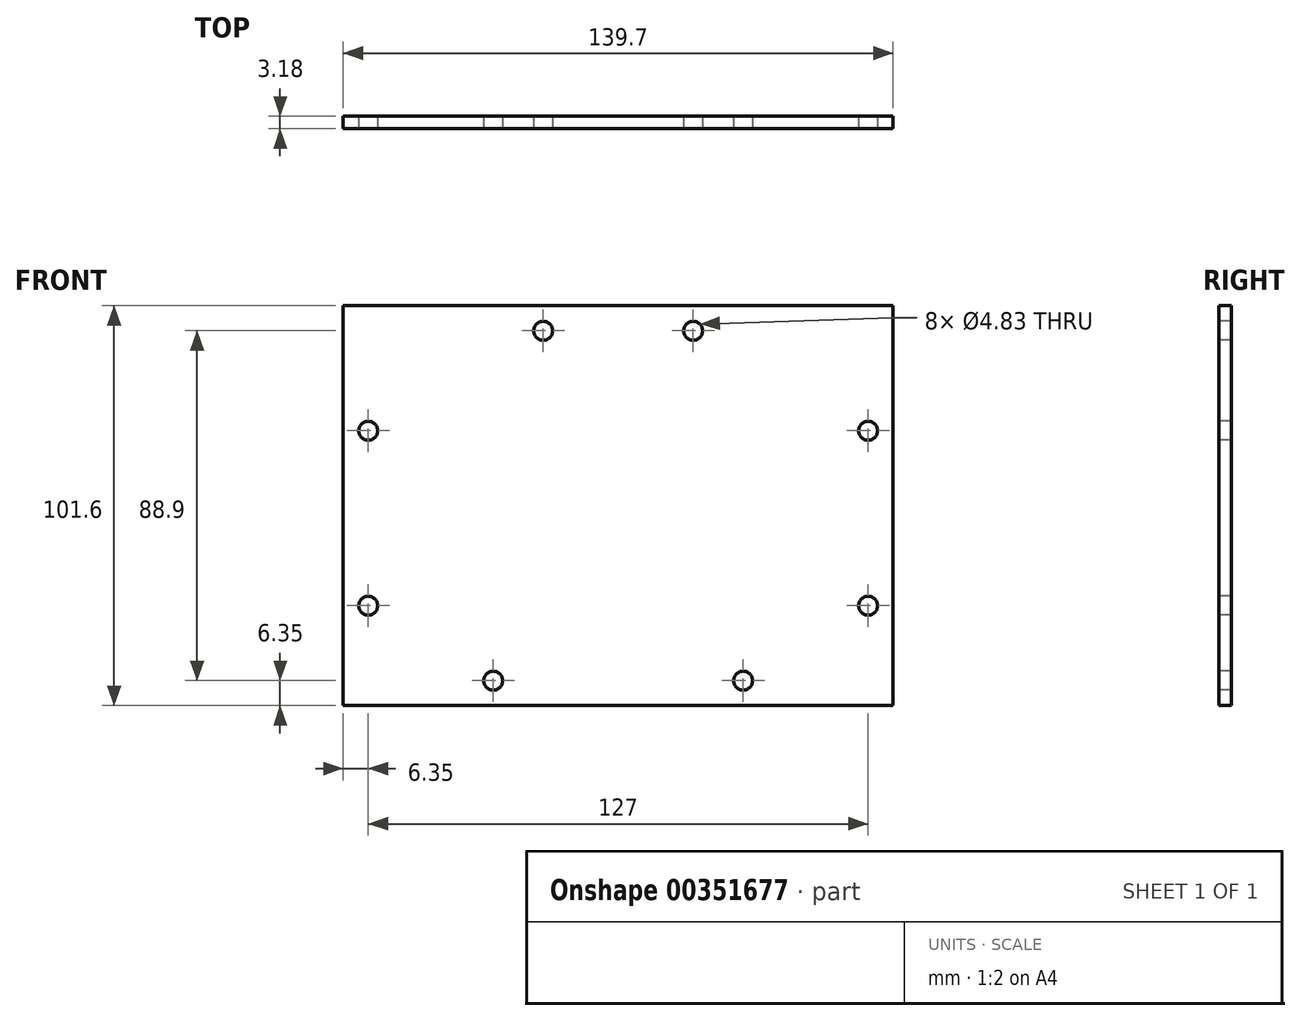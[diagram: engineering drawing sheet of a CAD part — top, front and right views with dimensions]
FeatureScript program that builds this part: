
annotation { "Feature Type Name" : "Feature", "Feature Type Description" : "" }
export const myFeature = defineFeature(function(context is Context, id is Id, definition is map)
    precondition{}
    {
        {
            var Q0;
            Q0=qCreatedBy(makeId("Front.planeOp"),FACE);
            var sketch = newSketch(context, id + "F0", { "sketchPlane" : qUnion([Q0])});
            skLineSegment(sketch, "E0.bottom", {"start": v(-69.85, 50.8) * mm, "end": v(69.85, 50.8) * mm});
            skLineSegment(sketch, "E0.top", {"start": v(-69.85, -50.8) * mm, "end": v(69.85, -50.8) * mm});
            skLineSegment(sketch, "E0.left", {"start": v(-69.85, 50.8) * mm, "end": v(-69.85, -50.8) * mm});
            skLineSegment(sketch, "E0.right", {"start": v(69.85, 50.8) * mm, "end": v(69.85, -50.8) * mm});
            skPoint(sketch, "E0.middle", {"position": v(0, 0) * mm});
            skSolve(sketch);
        }
        {
            var Q0;
            Q0 = qSketchRegion(id + "F0", true);
            extrude(context, id + "F1", {"entities" : qUnion([Q0]), "endBound" : BoundingType.SYMMETRIC, "depth" : 3.17 * mm});
        }
        {
            var Q0;
            Q0=makeQuery(id+"F1.opExtrude","CAP_FACE",FACE,{"disambiguationData":[OSD([sQuery(id+"F0.wireOp",EDGE,"E0.bottom"),sQuery(id+"F0.wireOp",EDGE,"E0.top"),sQuery(id+"F0.wireOp",EDGE,"E0.left"),sQuery(id+"F0.wireOp",EDGE,"E0.right")])],"isStart":false});
            var sketch = newSketch(context, id + "F2", { "sketchPlane" : qUnion([Q0])});
            skCircle(sketch, "E1", {"center": v(-19.05, 44.45) * mm, "radius": 2.41 * mm});
            skCircle(sketch, "E2", {"center": v(19.05, 44.45) * mm, "radius": 2.41 * mm});
            skSolve(sketch);
        }
        {
            var Q0;
            Q0 = qSketchRegion(id + "F2", true);
            extrude(context, id + "F3", {"entities" : qUnion([Q0]), "operationType" : NewBodyOperationType.REMOVE, "oppositeDirection" : true, "depth" : 3.17 * mm});
        }
        {
            var Q0;
            Q0=makeQuery(id+"F1.opExtrude","CAP_FACE",FACE,{"disambiguationData":[OSD([sQuery(id+"F0.wireOp",EDGE,"E0.bottom"),sQuery(id+"F0.wireOp",EDGE,"E0.top"),sQuery(id+"F0.wireOp",EDGE,"E0.left"),sQuery(id+"F0.wireOp",EDGE,"E0.right")])],"isStart":false});
            var sketch = newSketch(context, id + "F4", { "sketchPlane" : qUnion([Q0])});
            skCircle(sketch, "E3", {"center": v(63.5, 19.05) * mm, "radius": 2.41 * mm});
            skCircle(sketch, "E4", {"center": v(63.5, -25.4) * mm, "radius": 2.41 * mm});
            skSolve(sketch);
        }
        {
            var Q0;
            Q0 = qSketchRegion(id + "F4", true);
            extrude(context, id + "F5", {"entities" : qUnion([Q0]), "operationType" : NewBodyOperationType.REMOVE, "oppositeDirection" : true, "depth" : 3.17 * mm});
        }
        {
            var Q0;
            Q0=makeQuery(id+"F1.opExtrude","CAP_FACE",FACE,{"disambiguationData":[OSD([sQuery(id+"F0.wireOp",EDGE,"E0.bottom"),sQuery(id+"F0.wireOp",EDGE,"E0.top"),sQuery(id+"F0.wireOp",EDGE,"E0.left"),sQuery(id+"F0.wireOp",EDGE,"E0.right")])],"isStart":false});
            var sketch = newSketch(context, id + "F6", { "sketchPlane" : qUnion([Q0])});
            skCircle(sketch, "E5", {"center": v(-31.75, -44.45) * mm, "radius": 2.41 * mm});
            skSolve(sketch);
        }
        {
            var Q0;
            Q0=makeQuery(id+"F6.imprint","IMPRINT",FACE,{"disambiguationData":[TD([[makeQuery(id+"F6.imprint","IMPRINT",EDGE,{"derivedFrom":sQuery(id+"F6.wireOp",EDGE,"E5")}),-1.0]])]});
            var sketch = newSketch(context, id + "F7", { "sketchPlane" : qUnion([Q0])});
            skCircle(sketch, "E6", {"center": v(31.75, -44.45) * mm, "radius": 2.41 * mm});
            skSolve(sketch);
        }
        {
            var Q0;
            Q0 = qSketchRegion(id + "F6", true);
            extrude(context, id + "F8", {"entities" : qUnion([Q0]), "operationType" : NewBodyOperationType.REMOVE, "oppositeDirection" : true, "depth" : 3.17 * mm});
        }
        {
            var Q0;
            Q0 = qSketchRegion(id + "F7", true);
            extrude(context, id + "F9", {"entities" : qUnion([Q0]), "operationType" : NewBodyOperationType.REMOVE, "oppositeDirection" : true, "depth" : 3.17 * mm});
        }
        {
            var Q0;
            Q0=makeQuery(id+"F1.opExtrude","CAP_FACE",FACE,{"disambiguationData":[OSD([sQuery(id+"F0.wireOp",EDGE,"E0.bottom"),sQuery(id+"F0.wireOp",EDGE,"E0.top"),sQuery(id+"F0.wireOp",EDGE,"E0.left"),sQuery(id+"F0.wireOp",EDGE,"E0.right")])],"isStart":false});
            var sketch = newSketch(context, id + "F10", { "sketchPlane" : qUnion([Q0])});
            skCircle(sketch, "E7", {"center": v(-63.5, 19.05) * mm, "radius": 2.41 * mm});
            skSolve(sketch);
        }
        {
            var Q0;
            Q0=makeQuery(id+"F10.imprint","IMPRINT",FACE,{"disambiguationData":[TD([[makeQuery(id+"F10.imprint","IMPRINT",EDGE,{"derivedFrom":sQuery(id+"F10.wireOp",EDGE,"E7")}),-1.0]])]});
            var sketch = newSketch(context, id + "F11", { "sketchPlane" : qUnion([Q0])});
            skCircle(sketch, "E8", {"center": v(-63.5, -25.4) * mm, "radius": 2.41 * mm});
            skSolve(sketch);
        }
        {
            var Q0;
            Q0 = qSketchRegion(id + "F10", true);
            extrude(context, id + "F12", {"entities" : qUnion([Q0]), "operationType" : NewBodyOperationType.REMOVE, "oppositeDirection" : true, "depth" : 3.17 * mm});
        }
        {
            var Q0;
            Q0 = qSketchRegion(id + "F11", true);
            extrude(context, id + "F13", {"entities" : qUnion([Q0]), "operationType" : NewBodyOperationType.REMOVE, "oppositeDirection" : true, "depth" : 3.17 * mm});
        }
    });
